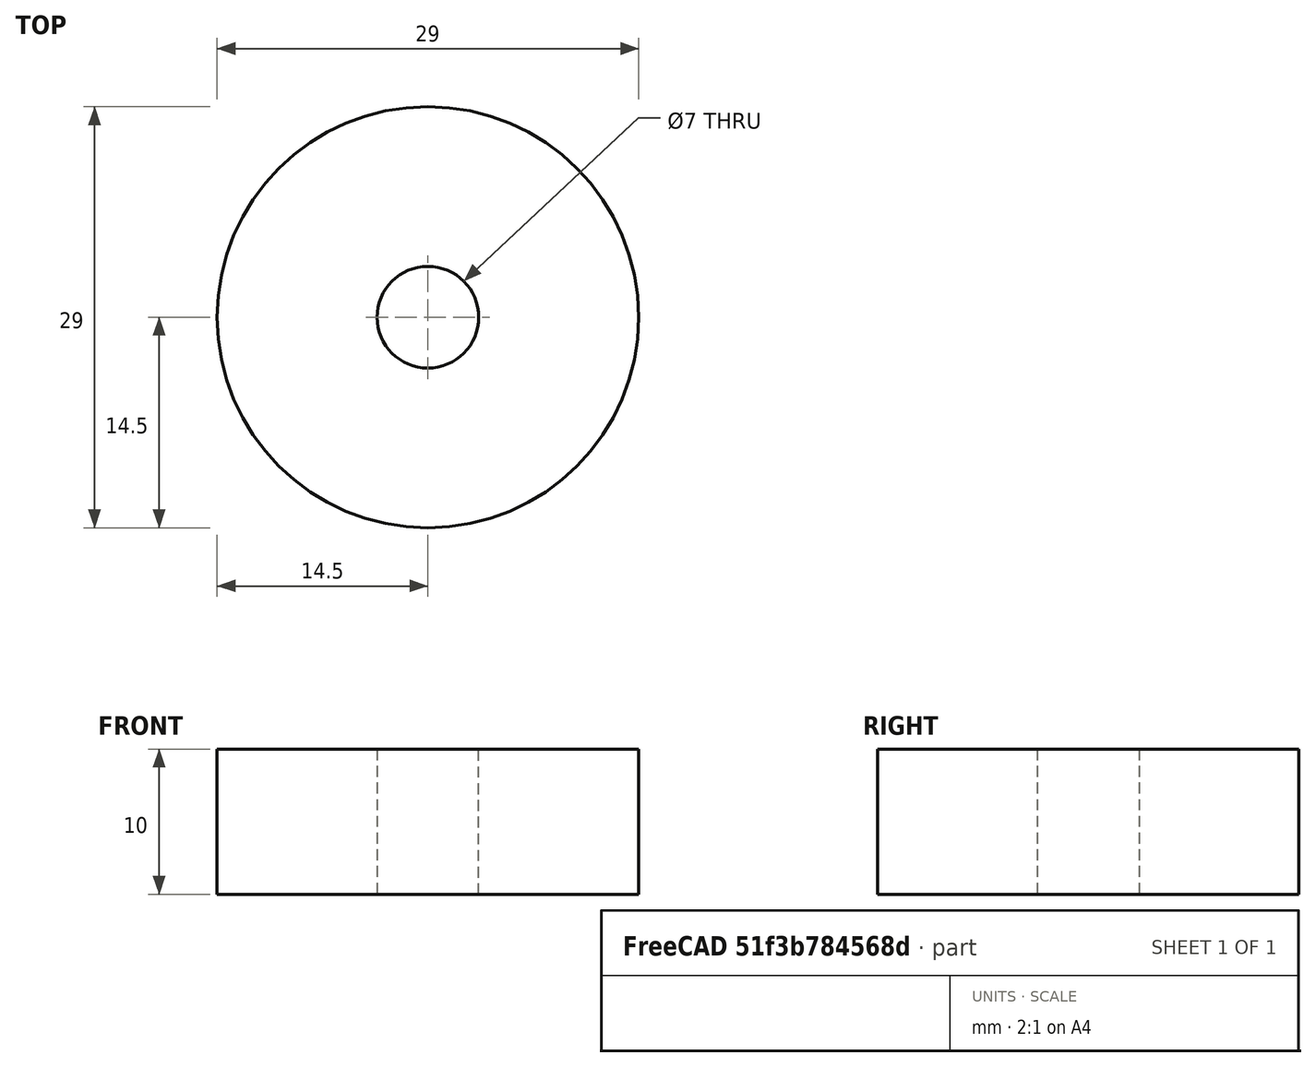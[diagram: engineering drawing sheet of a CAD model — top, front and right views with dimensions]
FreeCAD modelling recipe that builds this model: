
FCSTD DOCUMENT  (FreeCAD 0.20R29603 (Git))
Label: bread maker belt tighener press block
License: All rights reserved
LicenseURL: http://en.wikipedia.org/wiki/All_rights_reserved
objects: Sketcher::SketchObject×1, PartDesign::Pad×1, PartDesign::Body×1
note: 4 computed .brp shape members not serialized (recipe doc carries the construction recipe); baked Part::Feature solids carry a one-line shape summary decoded from their .brp

FEATURE [Sketcher::SketchObject] Sketch
  FullyConstrained = true
  MapMode = 5
  Support = -> [XY_Plane]
  sketch-geometry (2):
    g0: Circle CenterX=0 CenterY=0 CenterZ=0 NormalX=0 NormalY=0 NormalZ=1 AngleXU=0 Radius=3.5
    g1: Circle CenterX=0 CenterY=0 CenterZ=0 NormalX=0 NormalY=0 NormalZ=1 AngleXU=0 Radius=14.5
  constraints (4):
    c: Coincident(g0,g-1)
    c: Coincident(g1,g0)
    c: Diameter(g0) = 7
    c: Diameter(g1) = 29
FEATURE [PartDesign::Pad] Pad
  Direction = (0,0,1)
  Length = 10
  Length2 = 10
  Profile = -> Sketch
  ReferenceAxis = -> Sketch [N_Axis]
  Type = 0
FEATURE [PartDesign::Body] Body
  Group = -> [Sketch,Pad]
  Origin = -> Origin
  Tip = -> Pad
